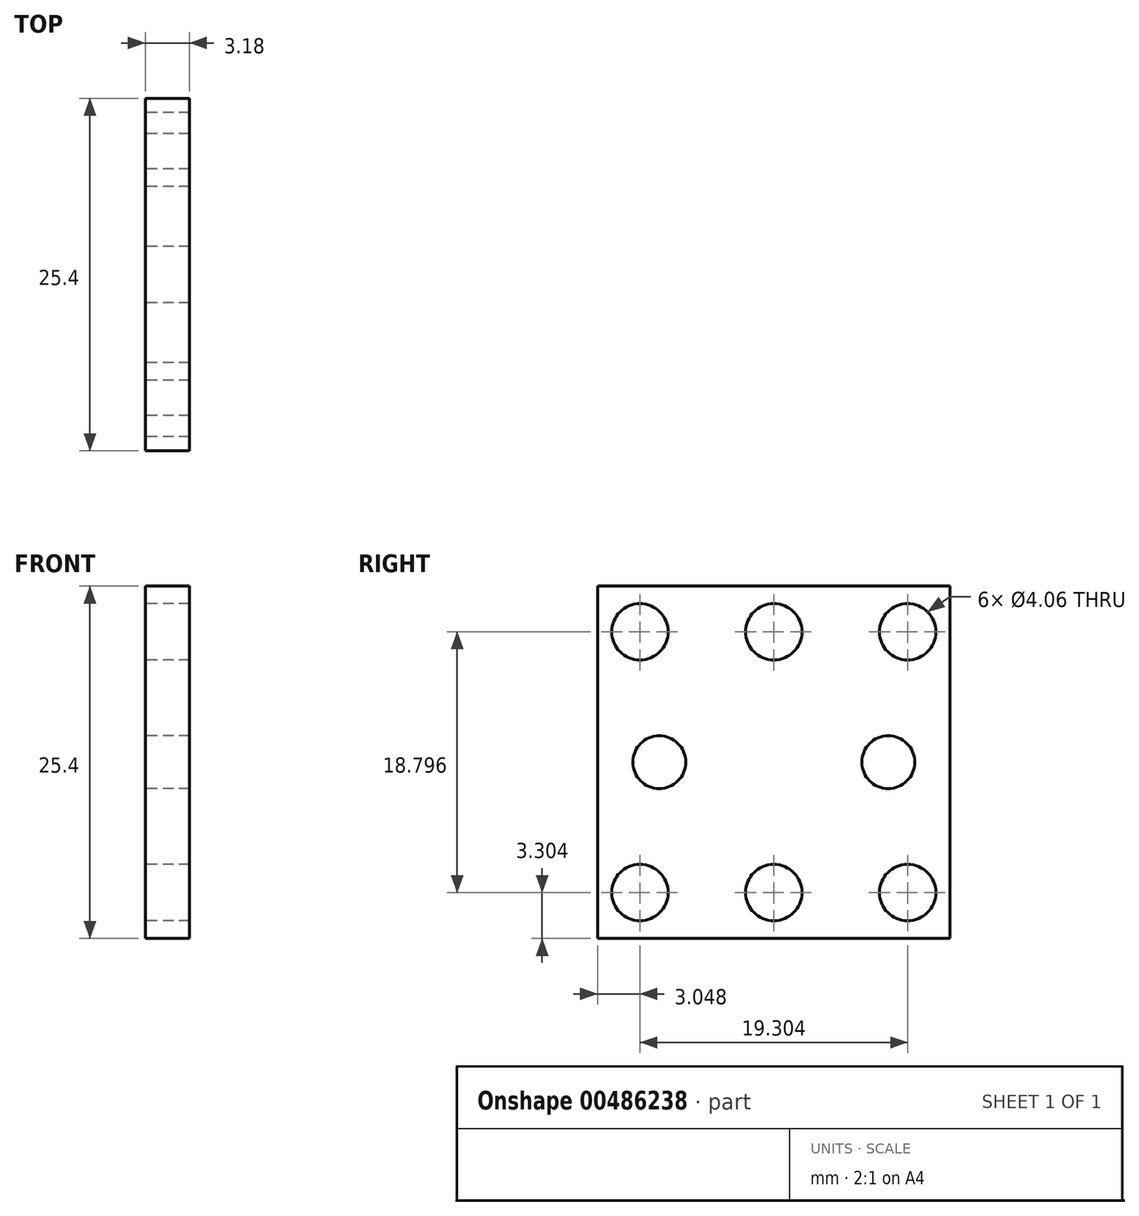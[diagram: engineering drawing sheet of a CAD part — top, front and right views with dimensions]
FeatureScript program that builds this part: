
annotation { "Feature Type Name" : "Feature", "Feature Type Description" : "" }
export const myFeature = defineFeature(function(context is Context, id is Id, definition is map)
    precondition{}
    {
        {
            var Q0;
            Q0=qCreatedBy(makeId("Right.planeOp"),FACE);
            var sketch = newSketch(context, id + "F0", { "sketchPlane" : qUnion([Q0])});
            skLineSegment(sketch, "E0.bottom", {"start": v(12.7, 11.02) * mm, "end": v(-12.7, 11.02) * mm});
            skLineSegment(sketch, "E0.top", {"start": v(12.7, -14.38) * mm, "end": v(-12.7, -14.38) * mm});
            skLineSegment(sketch, "E0.left", {"start": v(12.7, 11.02) * mm, "end": v(12.7, -14.38) * mm});
            skLineSegment(sketch, "E0.right", {"start": v(-12.7, 11.02) * mm, "end": v(-12.7, -14.38) * mm});
            skPoint(sketch, "E0.middle", {"position": v(0, -1.68) * mm});
            skLineSegment(sketch, "E1", {"start": v(0, 11.02) * mm, "end": v(0, -14.38) * mm, "construction": true});
            skLineSegment(sketch, "E2", {"start": v(0, -14.38) * mm, "end": v(0, 11.02) * mm, "construction": true});
            skLineSegment(sketch, "E3", {"start": v(0, 11.02) * mm, "end": v(0, 7.72) * mm, "construction": true});
            skLineSegment(sketch, "E4", {"start": v(0, 7.72) * mm, "end": v(0, -11.08) * mm, "construction": true});
            skCircle(sketch, "E5", {"center": v(0, 7.72) * mm, "radius": 2.03 * mm});
            skCircle(sketch, "E6", {"center": v(0, -11.08) * mm, "radius": 2.03 * mm});
            skLineSegment(sketch, "E7", {"start": v(0, 0) * mm, "end": v(0, -1.68) * mm, "construction": true});
            skLineSegment(sketch, "E8", {"start": v(0, 11.02) * mm, "end": v(0, -1.68) * mm, "construction": true});
            skLineSegment(sketch, "E9", {"start": v(12.7, -1.68) * mm, "end": v(-12.7, -1.68) * mm, "construction": true});
            skLineSegment(sketch, "E10", {"start": v(0, 7.72) * mm, "end": v(-9.65, 7.72) * mm, "construction": true});
            skLineSegment(sketch, "E11", {"start": v(-4.83, 7.72) * mm, "end": v(-4.83, 11.02) * mm, "construction": true});
            skCircle(sketch, "E12.MirrorC", {"center": v(-9.65, 7.72) * mm, "radius": 2.03 * mm});
            skCircle(sketch, "E13.MirrorC", {"center": v(-9.65, -11.08) * mm, "radius": 2.03 * mm});
            skCircle(sketch, "E14.MirrorC", {"center": v(9.65, 7.72) * mm, "radius": 2.03 * mm});
            skCircle(sketch, "E15.MirrorC", {"center": v(9.65, -11.08) * mm, "radius": 2.03 * mm});
            skSolve(sketch);
        }
        {
            var Q0;
            Q0 = qSketchRegion(id + "F0", true);
            extrude(context, id + "F1", {"entities" : qUnion([Q0]), "depth" : 3.17 * mm, "offsetDistance" : 25.4 * mm});
        }
        {
            var Q0;
            Q0=makeQuery(id+"F1.opExtrude","CAP_FACE",FACE,{"disambiguationData":[OSD([sQuery(id+"F0.wireOp",EDGE,"E0.bottom"),sQuery(id+"F0.wireOp",EDGE,"E0.top"),sQuery(id+"F0.wireOp",EDGE,"E0.left"),sQuery(id+"F0.wireOp",EDGE,"E0.right"),sQuery(id+"F0.wireOp",EDGE,"E5"),sQuery(id+"F0.wireOp",EDGE,"E6"),sQuery(id+"F0.wireOp",EDGE,"E12.MirrorC"),sQuery(id+"F0.wireOp",EDGE,"E13.MirrorC"),sQuery(id+"F0.wireOp",EDGE,"E14.MirrorC"),sQuery(id+"F0.wireOp",EDGE,"E15.MirrorC")])],"isStart":true});
            var sketch = newSketch(context, id + "F2", { "sketchPlane" : qUnion([Q0])});
            skLineSegment(sketch, "E16", {"start": v(0, 0) * mm, "end": v(6.35, 0) * mm, "construction": true});
            skLineSegment(sketch, "E17", {"start": v(6.35, 0) * mm, "end": v(-6.35, 0) * mm, "construction": true});
            skPoint(sketch, "E18.second.point", {"position": v(10.16, 0) * mm});
            skPoint(sketch, "E18.third.point", {"position": v(9.64, 1.3) * mm});
            skLineSegment(sketch, "E19", {"start": v(0, 0) * mm, "end": v(0, 2.54) * mm, "construction": true});
            skLineSegment(sketch, "E20", {"start": v(-10.16, 0) * mm, "end": v(10.16, 0) * mm, "construction": true});
            skLineSegment(sketch, "E21", {"start": v(-10.16, 0) * mm, "end": v(-12.7, 0) * mm, "construction": true});
            skLineSegment(sketch, "E22", {"start": v(-12.7, 0) * mm, "end": v(12.7, 0) * mm, "construction": true});
            skLineSegment(sketch, "E23", {"start": v(12.7, 0) * mm, "end": v(-10.16, 0) * mm, "construction": true});
            skLineSegment(sketch, "E24", {"start": v(-12.7, 0) * mm, "end": v(-10.16, 0) * mm, "construction": true});
            skLineSegment(sketch, "E25", {"start": v(10.16, 0) * mm, "end": v(12.7, 0) * mm, "construction": true});
            skLineSegment(sketch, "E26", {"start": v(6.35, 0) * mm, "end": v(10.16, 0) * mm, "construction": true});
            skLineSegment(sketch, "E27", {"start": v(0, 11.02) * mm, "end": v(0, -14.38) * mm, "construction": true});
            skLineSegment(sketch, "E28", {"start": v(0, -14.38) * mm, "end": v(0, -1.68) * mm, "construction": true});
            skLineSegment(sketch, "E29", {"start": v(0, -1.68) * mm, "end": v(0, 0) * mm, "construction": true});
            skLineSegment(sketch, "E30", {"start": v(0, -0.84) * mm, "end": v(2.94, -0.84) * mm, "construction": true});
            skCircle(sketch, "E31.MirrorC", {"center": v(8.26, -1.68) * mm, "radius": 1.9 * mm});
            skLineSegment(sketch, "E32.MirrorCS", {"start": v(-12.7, -1.68) * mm, "end": v(12.7, -1.68) * mm, "construction": true});
            skCircle(sketch, "E33.MirrorC", {"center": v(-8.26, -1.68) * mm, "radius": 1.9 * mm});
            skSolve(sketch);
        }
        {
            var Q0;
            Q0 = qSketchRegion(id + "F2", true);
            extrude(context, id + "F3", {"entities" : qUnion([Q0]), "operationType" : NewBodyOperationType.REMOVE, "oppositeDirection" : true, "depth" : 25.4 * mm, "offsetDistance" : 25.4 * mm});
        }
    });
